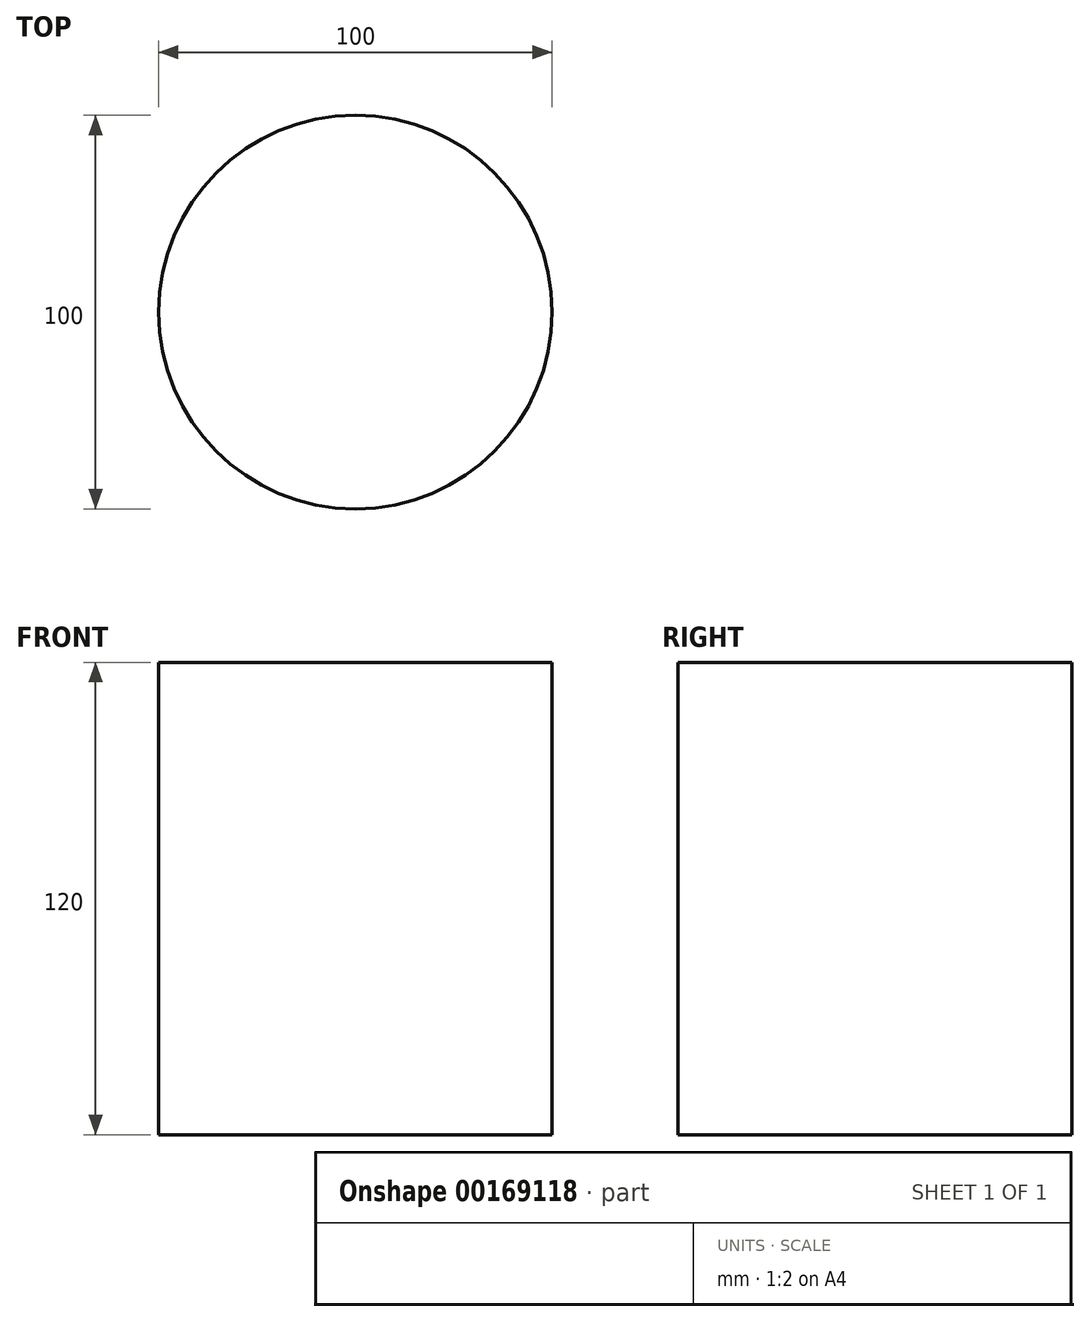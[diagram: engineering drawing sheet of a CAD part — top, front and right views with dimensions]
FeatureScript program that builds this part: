
annotation { "Feature Type Name" : "Feature", "Feature Type Description" : "" }
export const myFeature = defineFeature(function(context is Context, id is Id, definition is map)
    precondition{}
    {
        {
            var Q0;
            Q0=qCreatedBy(makeId("Top.planeOp"),FACE);
            var sketch = newSketch(context, id + "F0", { "sketchPlane" : qUnion([Q0])});
            skCircle(sketch, "E0", {"center": v(0, 0) * mm, "radius": 50 * mm});
            skSolve(sketch);
        }
        {
            var Q0;
            Q0=qSketchRegion(id+"F0",true);
            extrude(context, id + "F1", {"entities" : qUnion([Q0]), "depth" : 120 * mm});
        }
    });
